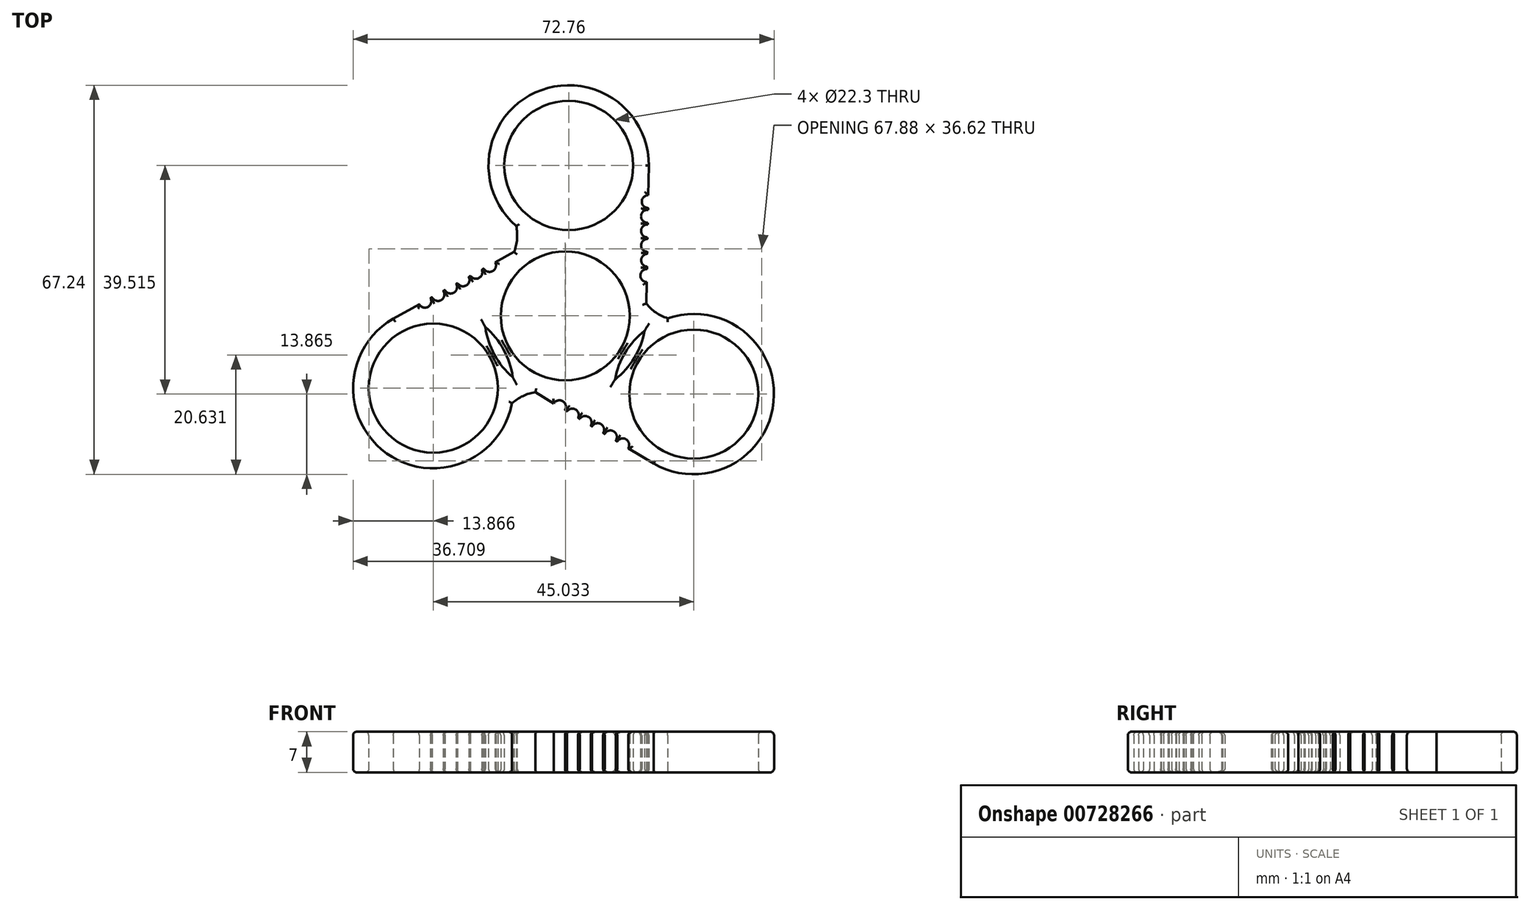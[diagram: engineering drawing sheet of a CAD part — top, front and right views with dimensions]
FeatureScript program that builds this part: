
annotation { "Feature Type Name" : "Feature", "Feature Type Description" : "" }
export const myFeature = defineFeature(function(context is Context, id is Id, definition is map)
    precondition{}
    {
        {
            var Q0;
            Q0=qCreatedBy(makeId("Top.planeOp"),FACE);
            var sketch = newSketch(context, id + "F0", { "sketchPlane" : qUnion([Q0])});
            skCircle(sketch, "E0", {"center": v(0, 0) * mm, "radius": 11.15 * mm});
            skCircle(sketch, "E1", {"center": v(0, 0) * mm, "radius": 13.96 * mm});
            skCircle(sketch, "E2", {"center": v(0.6, 26) * mm, "radius": 11.15 * mm});
            skCircle(sketch, "E3", {"center": v(0.6, 26) * mm, "radius": 13.86 * mm});
            skArc(sketch, "E4", {"start": v(-8.85, 11.06) * mm, "mid": v(-8.34, 13.26) * mm, "end": v(-8.48, 15.52) * mm});
            skLineSegment(sketch, "E5", {"start": v(14.46, 25.96) * mm, "end": v(14, 2.13) * mm});
            skCircle(sketch, "E6", {"center": v(14.34, 19.75) * mm, "radius": 1.12 * mm});
            skCircle(sketch, "E7", {"center": v(14.2, 17.22) * mm, "radius": 1.12 * mm});
            skCircle(sketch, "E8", {"center": v(14.22, 14.68) * mm, "radius": 1.12 * mm});
            skCircle(sketch, "E9", {"center": v(14.23, 12.19) * mm, "radius": 1.12 * mm});
            skCircle(sketch, "E10", {"center": v(14.24, 9.62) * mm, "radius": 1.12 * mm});
            skCircle(sketch, "E11", {"center": v(14.1, 6.98) * mm, "radius": 1.12 * mm});
            skCircle(sketch, "E12.1.0", {"center": v(-22.81, -12.48) * mm, "radius": 13.86 * mm});
            skLineSegment(sketch, "E12.1.3", {"start": v(-29.71, -0.46) * mm, "end": v(-8.85, 11.06) * mm});
            skCircle(sketch, "E12.1.4", {"center": v(-22.81, -12.48) * mm, "radius": 11.15 * mm});
            skArc(sketch, "E12.1.5", {"start": v(-5.16, -13.2) * mm, "mid": v(-7.32, -13.85) * mm, "end": v(-9.2, -15.1) * mm});
            skCircle(sketch, "E12.1.6", {"center": v(-15.45, 7.53) * mm, "radius": 1.12 * mm});
            skCircle(sketch, "E12.1.7", {"center": v(-24.28, 2.54) * mm, "radius": 1.12 * mm});
            skCircle(sketch, "E12.1.8", {"center": v(-22.02, 3.7) * mm, "radius": 1.12 * mm});
            skCircle(sketch, "E12.1.9", {"center": v(-13.1, 8.72) * mm, "radius": 1.12 * mm});
            skCircle(sketch, "E12.1.10", {"center": v(-17.67, 6.23) * mm, "radius": 1.12 * mm});
            skCircle(sketch, "E12.1.11", {"center": v(-19.82, 4.98) * mm, "radius": 1.12 * mm});
            skCircle(sketch, "E12.2.0", {"center": v(22.22, -13.52) * mm, "radius": 13.86 * mm});
            skLineSegment(sketch, "E12.2.3", {"start": v(15.26, -25.5) * mm, "end": v(-5.16, -13.2) * mm});
            skCircle(sketch, "E12.2.4", {"center": v(22.22, -13.52) * mm, "radius": 11.15 * mm});
            skArc(sketch, "E12.2.5", {"start": v(14, 2.13) * mm, "mid": v(15.66, 0.59) * mm, "end": v(17.68, -0.42) * mm});
            skCircle(sketch, "E12.2.6", {"center": v(1.2, -17.14) * mm, "radius": 1.12 * mm});
            skCircle(sketch, "E12.2.7", {"center": v(9.94, -22.3) * mm, "radius": 1.12 * mm});
            skCircle(sketch, "E12.2.8", {"center": v(7.8, -20.92) * mm, "radius": 1.12 * mm});
            skCircle(sketch, "E12.2.9", {"center": v(-1, -15.7) * mm, "radius": 1.12 * mm});
            skCircle(sketch, "E12.2.10", {"center": v(3.44, -18.42) * mm, "radius": 1.12 * mm});
            skCircle(sketch, "E12.2.11", {"center": v(5.6, -19.66) * mm, "radius": 1.12 * mm});
            skPoint(sketch, "E13.orphan", {"position": v(13.96, 0) * mm});
            skPoint(sketch, "E14.orphan", {"position": v(13.74, 2.48) * mm});
            skPoint(sketch, "E15.orphan", {"position": v(-4.72, -13.14) * mm});
            skPoint(sketch, "E16.orphan", {"position": v(-6.98, -12.1) * mm});
            skPoint(sketch, "E17.orphan", {"position": v(-6.98, 12.1) * mm});
            skPoint(sketch, "E18.orphan", {"position": v(-9.02, 10.65) * mm});
            skSolve(sketch);
        }
        {
            var Q0;
            {var subQ13=sQuery(id+"F0.wireOp",EDGE,"E1");var subQ15=makeQuery(id+"F0.imprint","IMPRINT",VERTEX,{"disambiguationData":[OD(0.0)],"derivedFrom":subQ13});Q0=makeQuery(id+"F0.imprint","IMPRINT",FACE,{"disambiguationData":[TD([[makeQuery(id+"F0.imprint","IMPRINT",EDGE,{"disambiguationData":[TD([[subQ15,-1.0]])],"derivedFrom":subQ13}),-1.0]])]});}
            var Q1;
            {var subQ20=sQuery(id+"F0.wireOp",EDGE,"E1");var subQ23=makeQuery(id+"F0.imprint","IMPRINT",VERTEX,{"disambiguationData":[OD(1.0)],"derivedFrom":subQ20});Q1=makeQuery(id+"F0.imprint","IMPRINT",FACE,{"disambiguationData":[TD([[makeQuery(id+"F0.imprint","IMPRINT",EDGE,{"disambiguationData":[TD([[subQ23,1.0]])],"derivedFrom":subQ20}),-1.0]])]});}
            var Q2;
            Q2=makeQuery(id+"F0.imprint","IMPRINT",FACE,{"disambiguationData":[TD([[makeQuery(id+"F0.imprint","IMPRINT",EDGE,{"derivedFrom":sQuery(id+"F0.wireOp",EDGE,"E2")}),-1.0]])]});
            var Q3;
            Q3=makeQuery(id+"F0.imprint","IMPRINT",FACE,{"disambiguationData":[TD([[makeQuery(id+"F0.imprint","IMPRINT",EDGE,{"derivedFrom":sQuery(id+"F0.wireOp",EDGE,"E0")}),-1.0]])]});
            var Q4;
            {var subQ24=sQuery(id+"F0.wireOp",EDGE,"E1");var subQ27=makeQuery(id+"F0.imprint","IMPRINT",VERTEX,{"disambiguationData":[OD(2.0)],"derivedFrom":subQ24});Q4=makeQuery(id+"F0.imprint","IMPRINT",FACE,{"disambiguationData":[TD([[makeQuery(id+"F0.imprint","IMPRINT",EDGE,{"disambiguationData":[TD([[subQ27,1.0]])],"derivedFrom":subQ24}),-1.0]])]});}
            var Q5;
            {var subQ0=sQuery(id+"F0.wireOp",EDGE,"E1");var subQ1=sQuery(id+"F0.wireOp",EDGE,"E5");var subQ2=makeQuery(id+"F0.imprint","INTERSECT",VERTEX,{"derivedFrom":[subQ1,subQ0]});Q5=makeQuery(id+"F0.imprint","IMPRINT",FACE,{"disambiguationData":[TD([[makeQuery(id+"F0.imprint","IMPRINT",EDGE,{"disambiguationData":[TD([[subQ2,1.0]])],"derivedFrom":subQ1}),-1.0]])]});}
            var Q6;
            {var subQ0=sQuery(id+"F0.wireOp",EDGE,"E12.2.3");var subQ1=sQuery(id+"F0.wireOp",EDGE,"E12.2.0");var subQ2=makeQuery(id+"F0.imprint","INTERSECT",VERTEX,{"disambiguationData":[OD(0.0)],"derivedFrom":[subQ1,subQ0]});Q6=makeQuery(id+"F0.imprint","IMPRINT",FACE,{"disambiguationData":[TD([[makeQuery(id+"F0.imprint","IMPRINT",EDGE,{"disambiguationData":[TD([[subQ2,1.0]])],"derivedFrom":subQ1}),1.0]])]});}
            var Q7;
            {var subQ0=sQuery(id+"F0.wireOp",EDGE,"E5");var subQ1=sQuery(id+"F0.wireOp",EDGE,"E3");var subQ2=makeQuery(id+"F0.imprint","INTERSECT",VERTEX,{"disambiguationData":[OD(0.0)],"derivedFrom":[subQ1,subQ0]});Q7=makeQuery(id+"F0.imprint","IMPRINT",FACE,{"disambiguationData":[TD([[makeQuery(id+"F0.imprint","IMPRINT",EDGE,{"disambiguationData":[TD([[subQ2,1.0]])],"derivedFrom":subQ1}),1.0]])]});}
            var Q8;
            {var subQ0=sQuery(id+"F0.wireOp",EDGE,"E12.1.3");var subQ1=sQuery(id+"F0.wireOp",EDGE,"E12.1.0");var subQ2=makeQuery(id+"F0.imprint","INTERSECT",VERTEX,{"disambiguationData":[OD(0.0)],"derivedFrom":[subQ1,subQ0]});Q8=makeQuery(id+"F0.imprint","IMPRINT",FACE,{"disambiguationData":[TD([[makeQuery(id+"F0.imprint","IMPRINT",EDGE,{"disambiguationData":[TD([[subQ2,1.0]])],"derivedFrom":subQ1}),1.0]])]});}
            var Q9;
            {var subQ0=sQuery(id+"F0.wireOp",EDGE,"E1");var subQ1=sQuery(id+"F0.wireOp",EDGE,"E4");var subQ2=makeQuery(id+"F0.imprint","INTERSECT",VERTEX,{"derivedFrom":[subQ1,subQ0]});Q9=makeQuery(id+"F0.imprint","IMPRINT",FACE,{"disambiguationData":[TD([[makeQuery(id+"F0.imprint","IMPRINT",EDGE,{"disambiguationData":[TD([[subQ2,-1.0]])],"derivedFrom":subQ1}),-1.0]])]});}
            var Q10;
            {var subQ0=sQuery(id+"F0.wireOp",EDGE,"E1");var subQ1=sQuery(id+"F0.wireOp",EDGE,"E12.1.5");var subQ2=makeQuery(id+"F0.imprint","INTERSECT",VERTEX,{"derivedFrom":[subQ1,subQ0]});Q10=makeQuery(id+"F0.imprint","IMPRINT",FACE,{"disambiguationData":[TD([[makeQuery(id+"F0.imprint","IMPRINT",EDGE,{"disambiguationData":[TD([[subQ2,-1.0]])],"derivedFrom":subQ1}),-1.0]])]});}
            var Q11;
            Q11=makeQuery(id+"F0.imprint","IMPRINT",FACE,{"disambiguationData":[TD([[makeQuery(id+"F0.imprint","IMPRINT",EDGE,{"derivedFrom":sQuery(id+"F0.wireOp",EDGE,"E12.1.4")}),-1.0]])]});
            var Q12;
            Q12=makeQuery(id+"F0.imprint","IMPRINT",FACE,{"disambiguationData":[TD([[makeQuery(id+"F0.imprint","IMPRINT",EDGE,{"derivedFrom":sQuery(id+"F0.wireOp",EDGE,"E12.2.4")}),-1.0]])]});
            var Q13;
            {var subQ0=sQuery(id+"F0.wireOp",EDGE,"E1");var subQ1=sQuery(id+"F0.wireOp",EDGE,"E3");var subQ2=makeQuery(id+"F0.imprint","INTERSECT",VERTEX,{"disambiguationData":[OD(0.0)],"derivedFrom":[subQ1,subQ0]});Q13=makeQuery(id+"F0.imprint","IMPRINT",FACE,{"disambiguationData":[TD([[makeQuery(id+"F0.imprint","IMPRINT",EDGE,{"disambiguationData":[TD([[subQ2,-1.0]])],"derivedFrom":subQ1}),1.0]])]});}
            var Q14;
            {var subQ0=sQuery(id+"F0.wireOp",EDGE,"E1");var subQ1=sQuery(id+"F0.wireOp",EDGE,"E12.2.0");var subQ2=makeQuery(id+"F0.imprint","INTERSECT",VERTEX,{"disambiguationData":[OD(0.0)],"derivedFrom":[subQ1,subQ0]});Q14=makeQuery(id+"F0.imprint","IMPRINT",FACE,{"disambiguationData":[TD([[makeQuery(id+"F0.imprint","IMPRINT",EDGE,{"disambiguationData":[TD([[subQ2,-1.0]])],"derivedFrom":subQ1}),1.0]])]});}
            var Q15;
            {var subQ0=sQuery(id+"F0.wireOp",EDGE,"E1");var subQ1=sQuery(id+"F0.wireOp",EDGE,"E12.1.0");var subQ2=makeQuery(id+"F0.imprint","INTERSECT",VERTEX,{"disambiguationData":[OD(0.0)],"derivedFrom":[subQ1,subQ0]});Q15=makeQuery(id+"F0.imprint","IMPRINT",FACE,{"disambiguationData":[TD([[makeQuery(id+"F0.imprint","IMPRINT",EDGE,{"disambiguationData":[TD([[subQ2,-1.0]])],"derivedFrom":subQ1}),1.0]])]});}
            extrude(context, id + "F1", {"entities" : qUnion([Q0, Q1, Q2, Q3, Q4, Q5, Q6, Q7, Q8, Q9, Q10, Q11, Q12, Q13, Q14, Q15]), "depth" : 7 * mm, "offsetDistance" : 25 * mm});
        }
        {
            var Q0;
            Q0=makeQuery(id+"F1.opExtrude","CAP_EDGE",EDGE,{"disambiguationData":[OSD([sQuery(id+"F0.wireOp",EDGE,"E12.1.5")])],"isStart":false});
            var Q1;
            {var subQ0=sQuery(id+"F0.wireOp",EDGE,"E12.2.3");Q1=makeQuery(id+"F1.opExtrude","CAP_EDGE",EDGE,{"disambiguationData":[OSD([subQ0]),TDD([makeQuery(id+"F0.imprint","IMPRINT",EDGE,{"disambiguationData":[TD([[makeQuery(id+"F0.imprint","INTERSECT",VERTEX,{"derivedFrom":[sQuery(id+"F0.wireOp",EDGE,"E12.1.5"),subQ0]}),1.0]])],"derivedFrom":subQ0})])],"isStart":false});}
            var Q2;
            Q2=makeQuery(id+"F1.opExtrude","CAP_EDGE",EDGE,{"disambiguationData":[OSD([sQuery(id+"F0.wireOp",EDGE,"E12.1.0")])],"isStart":false});
            var Q3;
            Q3=makeQuery(id+"F1.opExtrude","CAP_EDGE",EDGE,{"disambiguationData":[OSD([sQuery(id+"F0.wireOp",EDGE,"E12.1.0")])],"isStart":true});
            var Q4;
            {var subQ0=sQuery(id+"F0.wireOp",EDGE,"E12.1.3");Q4=makeQuery(id+"F1.opExtrude","CAP_EDGE",EDGE,{"disambiguationData":[OSD([subQ0]),TDD([makeQuery(id+"F0.imprint","IMPRINT",EDGE,{"disambiguationData":[TD([[makeQuery(id+"F0.imprint","INTERSECT",VERTEX,{"disambiguationData":[OD(1.0)],"derivedFrom":[sQuery(id+"F0.wireOp",EDGE,"E12.1.0"),subQ0]}),-1.0]])],"derivedFrom":subQ0})])],"isStart":true});}
            var Q5;
            {var subQ0=sQuery(id+"F0.wireOp",EDGE,"E12.1.3");Q5=makeQuery(id+"F1.opExtrude","CAP_EDGE",EDGE,{"disambiguationData":[OSD([subQ0]),TDD([makeQuery(id+"F0.imprint","IMPRINT",EDGE,{"disambiguationData":[TD([[makeQuery(id+"F0.imprint","INTERSECT",VERTEX,{"disambiguationData":[OD(1.0)],"derivedFrom":[sQuery(id+"F0.wireOp",EDGE,"E12.1.0"),subQ0]}),-1.0]])],"derivedFrom":subQ0})])],"isStart":false});}
            var Q6;
            Q6=makeQuery(id+"F1.opExtrude","CAP_EDGE",EDGE,{"disambiguationData":[OSD([sQuery(id+"F0.wireOp",EDGE,"E12.1.5")])],"isStart":true});
            var Q7;
            {var subQ0=sQuery(id+"F0.wireOp",EDGE,"E12.2.3");Q7=makeQuery(id+"F1.opExtrude","CAP_EDGE",EDGE,{"disambiguationData":[OSD([subQ0]),TDD([makeQuery(id+"F0.imprint","IMPRINT",EDGE,{"disambiguationData":[TD([[makeQuery(id+"F0.imprint","INTERSECT",VERTEX,{"derivedFrom":[sQuery(id+"F0.wireOp",EDGE,"E12.1.5"),subQ0]}),1.0]])],"derivedFrom":subQ0})])],"isStart":true});}
            var Q8;
            Q8=makeQuery(id+"F1.opExtrude","CAP_EDGE",EDGE,{"disambiguationData":[OSD([sQuery(id+"F0.wireOp",EDGE,"E12.1.4")])],"isStart":false});
            var Q9;
            Q9=makeQuery(id+"F1.opExtrude","CAP_EDGE",EDGE,{"disambiguationData":[OSD([sQuery(id+"F0.wireOp",EDGE,"E12.1.4")])],"isStart":true});
            var Q10;
            Q10=makeQuery(id+"F1.opExtrude","CAP_EDGE",EDGE,{"disambiguationData":[OSD([sQuery(id+"F0.wireOp",EDGE,"E0")])],"isStart":true});
            var Q11;
            Q11=makeQuery(id+"F1.opExtrude","CAP_EDGE",EDGE,{"disambiguationData":[OSD([sQuery(id+"F0.wireOp",EDGE,"E0")])],"isStart":false});
            var Q12;
            {var subQ0=sQuery(id+"F0.wireOp",EDGE,"E12.1.3");Q12=makeQuery(id+"F1.opExtrude","CAP_EDGE",EDGE,{"disambiguationData":[OSD([subQ0]),TDD([makeQuery(id+"F0.imprint","IMPRINT",EDGE,{"disambiguationData":[TD([[makeQuery(id+"F0.imprint","INTERSECT",VERTEX,{"derivedFrom":[sQuery(id+"F0.wireOp",EDGE,"E4"),subQ0]}),1.0]])],"derivedFrom":subQ0})])],"isStart":false});}
            var Q13;
            Q13=makeQuery(id+"F1.opExtrude","CAP_EDGE",EDGE,{"disambiguationData":[OSD([sQuery(id+"F0.wireOp",EDGE,"E4")])],"isStart":false});
            var Q14;
            Q14=makeQuery(id+"F1.opExtrude","CAP_EDGE",EDGE,{"disambiguationData":[OSD([sQuery(id+"F0.wireOp",EDGE,"E3")])],"isStart":false});
            var Q15;
            Q15=makeQuery(id+"F1.opExtrude","CAP_EDGE",EDGE,{"disambiguationData":[OSD([sQuery(id+"F0.wireOp",EDGE,"E2")])],"isStart":false});
            var Q16;
            Q16=makeQuery(id+"F1.opExtrude","CAP_EDGE",EDGE,{"disambiguationData":[OSD([sQuery(id+"F0.wireOp",EDGE,"E2")])],"isStart":true});
            var Q17;
            Q17=makeQuery(id+"F1.opExtrude","CAP_EDGE",EDGE,{"disambiguationData":[OSD([sQuery(id+"F0.wireOp",EDGE,"E3")])],"isStart":true});
            var Q18;
            Q18=makeQuery(id+"F1.opExtrude","CAP_EDGE",EDGE,{"disambiguationData":[OSD([sQuery(id+"F0.wireOp",EDGE,"E4")])],"isStart":true});
            var Q19;
            {var subQ0=sQuery(id+"F0.wireOp",EDGE,"E12.1.3");Q19=makeQuery(id+"F1.opExtrude","CAP_EDGE",EDGE,{"disambiguationData":[OSD([subQ0]),TDD([makeQuery(id+"F0.imprint","IMPRINT",EDGE,{"disambiguationData":[TD([[makeQuery(id+"F0.imprint","INTERSECT",VERTEX,{"derivedFrom":[sQuery(id+"F0.wireOp",EDGE,"E4"),subQ0]}),1.0]])],"derivedFrom":subQ0})])],"isStart":true});}
            var Q20;
            Q20=makeQuery(id+"F1.opExtrude","CAP_EDGE",EDGE,{"disambiguationData":[OSD([sQuery(id+"F0.wireOp",EDGE,"E12.2.5")])],"isStart":false});
            var Q21;
            {var subQ0=sQuery(id+"F0.wireOp",EDGE,"E5");Q21=makeQuery(id+"F1.opExtrude","CAP_EDGE",EDGE,{"disambiguationData":[OSD([subQ0]),TDD([makeQuery(id+"F0.imprint","IMPRINT",EDGE,{"disambiguationData":[TD([[makeQuery(id+"F0.imprint","INTERSECT",VERTEX,{"disambiguationData":[OD(1.0)],"derivedFrom":[subQ0,sQuery(id+"F0.wireOp",EDGE,"E11")]}),-1.0]])],"derivedFrom":subQ0})])],"isStart":false});}
            var Q22;
            Q22=makeQuery(id+"F1.opExtrude","CAP_EDGE",EDGE,{"disambiguationData":[OSD([sQuery(id+"F0.wireOp",EDGE,"E12.2.0")])],"isStart":false});
            var Q23;
            Q23=makeQuery(id+"F1.opExtrude","CAP_EDGE",EDGE,{"disambiguationData":[OSD([sQuery(id+"F0.wireOp",EDGE,"E12.2.4")])],"isStart":false});
            var Q24;
            Q24=makeQuery(id+"F1.opExtrude","CAP_EDGE",EDGE,{"disambiguationData":[OSD([sQuery(id+"F0.wireOp",EDGE,"E12.2.4")])],"isStart":true});
            var Q25;
            Q25=makeQuery(id+"F1.opExtrude","CAP_EDGE",EDGE,{"disambiguationData":[OSD([sQuery(id+"F0.wireOp",EDGE,"E12.2.5")])],"isStart":true});
            var Q26;
            Q26=makeQuery(id+"F1.opExtrude","CAP_EDGE",EDGE,{"disambiguationData":[OSD([sQuery(id+"F0.wireOp",EDGE,"E12.2.0")])],"isStart":true});
            var Q27;
            Q27=makeQuery(id+"F1.opExtrude","CAP_EDGE",EDGE,{"disambiguationData":[OSD([sQuery(id+"F0.wireOp",EDGE,"E12.1.7")])],"isStart":false});
            var Q28;
            Q28=makeQuery(id+"F1.opExtrude","CAP_FACE",FACE,{"disambiguationData":[OSD([sQuery(id+"F0.wireOp",EDGE,"E2"),sQuery(id+"F0.wireOp",EDGE,"E3"),sQuery(id+"F0.wireOp",EDGE,"E4"),sQuery(id+"F0.wireOp",EDGE,"E5"),sQuery(id+"F0.wireOp",EDGE,"E6"),sQuery(id+"F0.wireOp",EDGE,"E7"),sQuery(id+"F0.wireOp",EDGE,"E8"),sQuery(id+"F0.wireOp",EDGE,"E9"),sQuery(id+"F0.wireOp",EDGE,"E10"),sQuery(id+"F0.wireOp",EDGE,"E11"),sQuery(id+"F0.wireOp",EDGE,"E12.1.0"),sQuery(id+"F0.wireOp",EDGE,"E12.1.3"),sQuery(id+"F0.wireOp",EDGE,"E12.1.4"),sQuery(id+"F0.wireOp",EDGE,"E12.1.5"),sQuery(id+"F0.wireOp",EDGE,"E12.1.6"),sQuery(id+"F0.wireOp",EDGE,"E12.1.7"),sQuery(id+"F0.wireOp",EDGE,"E12.1.8"),sQuery(id+"F0.wireOp",EDGE,"E12.1.9"),sQuery(id+"F0.wireOp",EDGE,"E12.1.10"),sQuery(id+"F0.wireOp",EDGE,"E12.1.11"),sQuery(id+"F0.wireOp",EDGE,"E12.2.0"),sQuery(id+"F0.wireOp",EDGE,"E0"),sQuery(id+"F0.wireOp",EDGE,"E12.2.3"),sQuery(id+"F0.wireOp",EDGE,"E12.2.4"),sQuery(id+"F0.wireOp",EDGE,"E12.2.5"),sQuery(id+"F0.wireOp",EDGE,"E12.2.6"),sQuery(id+"F0.wireOp",EDGE,"E12.2.7"),sQuery(id+"F0.wireOp",EDGE,"E12.2.8"),sQuery(id+"F0.wireOp",EDGE,"E12.2.9"),sQuery(id+"F0.wireOp",EDGE,"E12.2.10"),sQuery(id+"F0.wireOp",EDGE,"E12.2.11")])],"isStart":false});
            var Q29;
            Q29=makeQuery(id+"F1.opExtrude","CAP_EDGE",EDGE,{"disambiguationData":[OSD([sQuery(id+"F0.wireOp",EDGE,"E12.1.8")])],"isStart":false});
            var Q30;
            Q30=makeQuery(id+"F1.opExtrude","CAP_EDGE",EDGE,{"disambiguationData":[OSD([sQuery(id+"F0.wireOp",EDGE,"E12.1.11")])],"isStart":false});
            var Q31;
            Q31=makeQuery(id+"F1.opExtrude","CAP_EDGE",EDGE,{"disambiguationData":[OSD([sQuery(id+"F0.wireOp",EDGE,"E12.1.7")])],"isStart":true});
            var Q32;
            Q32=makeQuery(id+"F1.opExtrude","CAP_EDGE",EDGE,{"disambiguationData":[OSD([sQuery(id+"F0.wireOp",EDGE,"E12.1.8")])],"isStart":true});
            var Q33;
            Q33=makeQuery(id+"F1.opExtrude","CAP_EDGE",EDGE,{"disambiguationData":[OSD([sQuery(id+"F0.wireOp",EDGE,"E12.1.11")])],"isStart":true});
            var Q34;
            Q34=makeQuery(id+"F1.opExtrude","CAP_EDGE",EDGE,{"disambiguationData":[OSD([sQuery(id+"F0.wireOp",EDGE,"E12.1.10")])],"isStart":true});
            var Q35;
            Q35=makeQuery(id+"F1.opExtrude","CAP_EDGE",EDGE,{"disambiguationData":[OSD([sQuery(id+"F0.wireOp",EDGE,"E12.1.9")])],"isStart":true});
            var Q36;
            Q36=makeQuery(id+"F1.opExtrude","CAP_FACE",FACE,{"disambiguationData":[OSD([sQuery(id+"F0.wireOp",EDGE,"E2"),sQuery(id+"F0.wireOp",EDGE,"E3"),sQuery(id+"F0.wireOp",EDGE,"E4"),sQuery(id+"F0.wireOp",EDGE,"E5"),sQuery(id+"F0.wireOp",EDGE,"E6"),sQuery(id+"F0.wireOp",EDGE,"E7"),sQuery(id+"F0.wireOp",EDGE,"E8"),sQuery(id+"F0.wireOp",EDGE,"E9"),sQuery(id+"F0.wireOp",EDGE,"E10"),sQuery(id+"F0.wireOp",EDGE,"E11"),sQuery(id+"F0.wireOp",EDGE,"E12.1.0"),sQuery(id+"F0.wireOp",EDGE,"E12.1.3"),sQuery(id+"F0.wireOp",EDGE,"E12.1.4"),sQuery(id+"F0.wireOp",EDGE,"E12.1.5"),sQuery(id+"F0.wireOp",EDGE,"E12.1.6"),sQuery(id+"F0.wireOp",EDGE,"E12.1.7"),sQuery(id+"F0.wireOp",EDGE,"E12.1.8"),sQuery(id+"F0.wireOp",EDGE,"E12.1.9"),sQuery(id+"F0.wireOp",EDGE,"E12.1.10"),sQuery(id+"F0.wireOp",EDGE,"E12.1.11"),sQuery(id+"F0.wireOp",EDGE,"E12.2.0"),sQuery(id+"F0.wireOp",EDGE,"E0"),sQuery(id+"F0.wireOp",EDGE,"E12.2.3"),sQuery(id+"F0.wireOp",EDGE,"E12.2.4"),sQuery(id+"F0.wireOp",EDGE,"E12.2.5"),sQuery(id+"F0.wireOp",EDGE,"E12.2.6"),sQuery(id+"F0.wireOp",EDGE,"E12.2.7"),sQuery(id+"F0.wireOp",EDGE,"E12.2.8"),sQuery(id+"F0.wireOp",EDGE,"E12.2.9"),sQuery(id+"F0.wireOp",EDGE,"E12.2.10"),sQuery(id+"F0.wireOp",EDGE,"E12.2.11")])],"isStart":true});
            var Q37;
            Q37=makeQuery(id+"F1.opExtrude","CAP_EDGE",EDGE,{"disambiguationData":[OSD([sQuery(id+"F0.wireOp",EDGE,"E12.1.6")])],"isStart":true});
            fillet(context, id + "F2", {"entities" : qUnion([Q0, Q1, Q2, Q3, Q4, Q5, Q6, Q7, Q8, Q9, Q10, Q11, Q12, Q13, Q14, Q15, Q16, Q17, Q18, Q19, Q20, Q21, Q22, Q23, Q24, Q25, Q26, Q27, Q28, Q29, Q30, Q31, Q32, Q33, Q34, Q35, Q36, Q37]), "radius" : 0.6 * mm, "tangentPropagation" : true, "allowEdgeOverflow" : false});
        }
    });
